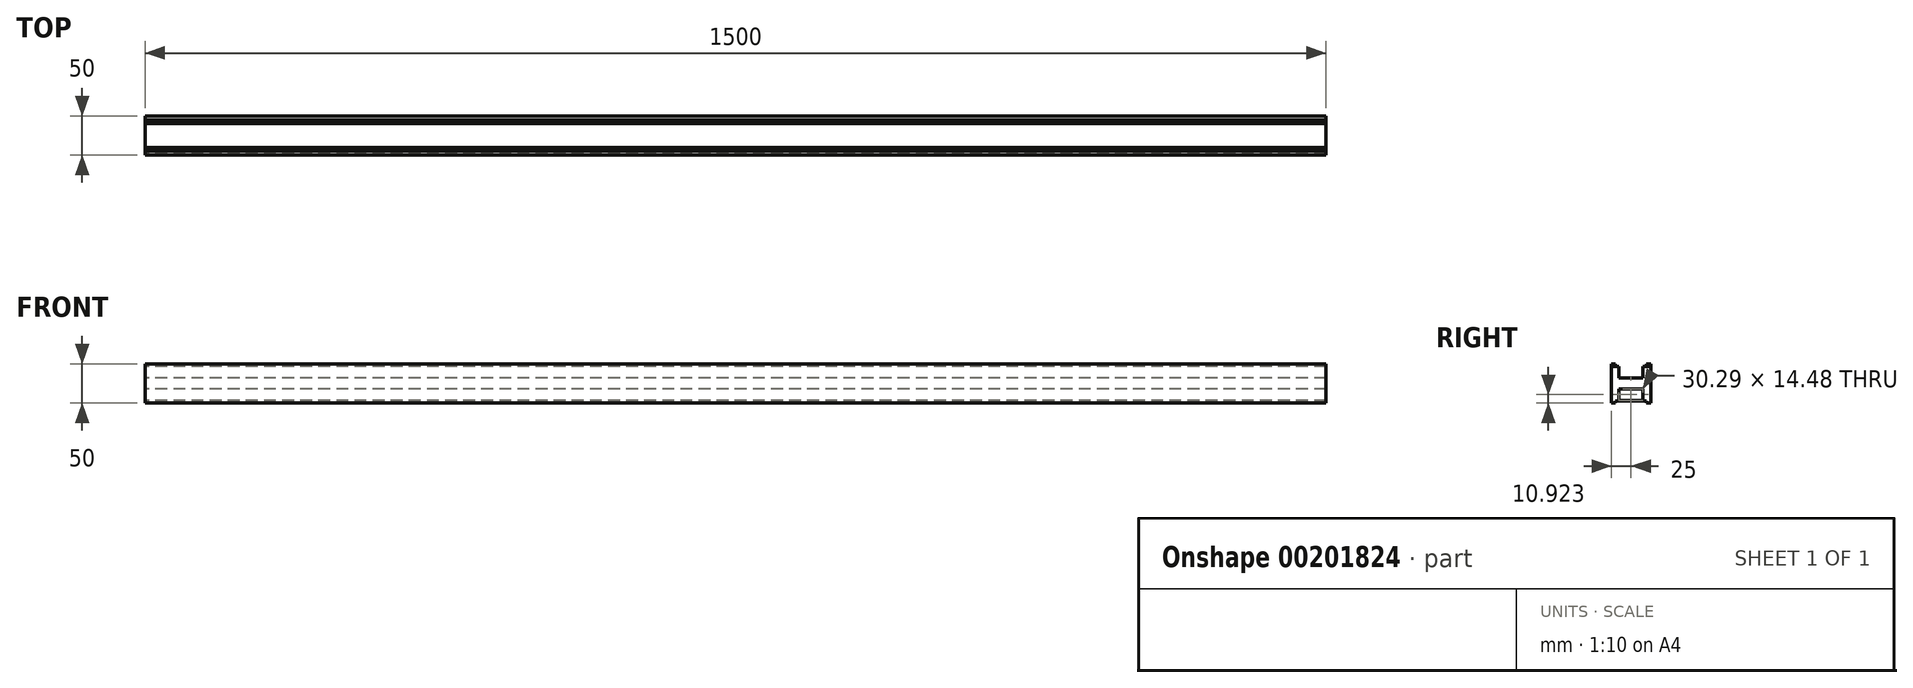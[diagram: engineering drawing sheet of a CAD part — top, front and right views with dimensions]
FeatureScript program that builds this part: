
annotation { "Feature Type Name" : "Feature", "Feature Type Description" : "" }
export const myFeature = defineFeature(function(context is Context, id is Id, definition is map)
    precondition{}
    {
        {
            var Q0;
            Q0=qCreatedBy(makeId("Right.planeOp"),FACE);
            var sketch = newSketch(context, id + "F0", { "sketchPlane" : qUnion([Q0])});
            skLineSegment(sketch, "E0.bottom", {"start": v(25, -25) * mm, "end": v(-25, -25) * mm});
            skLineSegment(sketch, "E0.top", {"start": v(25, 25) * mm, "end": v(-25, 25) * mm});
            skLineSegment(sketch, "E0.left", {"start": v(25, -25) * mm, "end": v(25, 25) * mm});
            skLineSegment(sketch, "E0.right", {"start": v(-25, -25) * mm, "end": v(-25, 25) * mm});
            skPoint(sketch, "E0.middle", {"position": v(0, 0) * mm});
            skSolve(sketch);
        }
        {
            var Q0;
            Q0 = qSketchRegion(id + "F0", true);
            var Q1;
            Q1=makeQuery(id+"F0.imprint","IMPRINT",FACE,{"disambiguationData":[TD([[makeQuery(id+"F0.imprint","IMPRINT",EDGE,{"derivedFrom":sQuery(id+"F0.wireOp",EDGE,"E0.bottom")}),-1.0]])]});
            extrude(context, id + "F1", {"entities" : qUnion([Q0, Q1]), "depth" : 1500 * mm, "offsetDistance" : 25 * mm});
        }
        {
            var Q0;
            Q0=makeQuery(id+"F1.opExtrude","CAP_FACE",FACE,{"disambiguationData":[OSD([sQuery(id+"F0.wireOp",EDGE,"E0.bottom"),sQuery(id+"F0.wireOp",EDGE,"E0.top"),sQuery(id+"F0.wireOp",EDGE,"E0.left"),sQuery(id+"F0.wireOp",EDGE,"E0.right")])],"isStart":true});
            var sketch = newSketch(context, id + "F2", { "sketchPlane" : qUnion([Q0])});
            skLineSegment(sketch, "E1.bottom", {"start": v(19.61, 22.47) * mm, "end": v(-19.61, 22.47) * mm});
            skLineSegment(sketch, "E1.top", {"start": v(19.61, 27.53) * mm, "end": v(-19.61, 27.53) * mm});
            skLineSegment(sketch, "E1.left", {"start": v(19.61, 22.47) * mm, "end": v(19.61, 27.53) * mm});
            skLineSegment(sketch, "E1.right", {"start": v(-19.61, 22.47) * mm, "end": v(-19.61, 27.53) * mm});
            skPoint(sketch, "E1.middle", {"position": v(0, 25) * mm});
            skLineSegment(sketch, "E2.bottom", {"start": v(23.38, 21.32) * mm, "end": v(-23.38, 21.32) * mm});
            skLineSegment(sketch, "E2.top", {"start": v(23.38, 23.62) * mm, "end": v(-23.38, 23.62) * mm});
            skLineSegment(sketch, "E2.left", {"start": v(23.38, 21.32) * mm, "end": v(23.38, 23.62) * mm});
            skLineSegment(sketch, "E2.right", {"start": v(-23.38, 21.32) * mm, "end": v(-23.38, 23.62) * mm});
            skPoint(sketch, "E2.middle", {"position": v(0, 22.47) * mm});
            skLineSegment(sketch, "E3.bottom", {"start": v(15.14, 6.84) * mm, "end": v(-15.14, 6.84) * mm});
            skLineSegment(sketch, "E3.top", {"start": v(15.14, 21.32) * mm, "end": v(-15.14, 21.32) * mm});
            skLineSegment(sketch, "E3.left", {"start": v(15.14, 6.84) * mm, "end": v(15.14, 21.32) * mm});
            skLineSegment(sketch, "E3.right", {"start": v(-15.14, 6.84) * mm, "end": v(-15.14, 21.32) * mm});
            skPoint(sketch, "E3.middle", {"position": v(0, 14.08) * mm});
            skPoint(sketch, "E3.middle.positionSnap0", {"position": v(0, 21.32) * mm});
            skPoint(sketch, "E3.centerSnap0", {"position": v(0, 21.32) * mm});
            skLineSegment(sketch, "E4", {"start": v(-25, 0) * mm, "end": v(25, 0) * mm, "construction": true});
            skLineSegment(sketch, "E5.MirrorCS", {"start": v(15.14, -6.84) * mm, "end": v(-15.14, -6.84) * mm});
            skLineSegment(sketch, "E6.MirrorCS", {"start": v(-15.14, -6.84) * mm, "end": v(-15.14, -21.32) * mm});
            skLineSegment(sketch, "E7.MirrorCS", {"start": v(15.14, -6.84) * mm, "end": v(15.14, -21.32) * mm});
            skLineSegment(sketch, "E8.MirrorCS", {"start": v(23.38, -21.32) * mm, "end": v(-23.38, -21.32) * mm});
            skLineSegment(sketch, "E9.MirrorCS", {"start": v(23.38, -21.32) * mm, "end": v(23.38, -23.62) * mm});
            skLineSegment(sketch, "E10.MirrorCS", {"start": v(23.38, -23.62) * mm, "end": v(-23.38, -23.62) * mm});
            skLineSegment(sketch, "E11.MirrorCS", {"start": v(19.61, -22.47) * mm, "end": v(19.61, -27.53) * mm});
            skLineSegment(sketch, "E12.MirrorCS", {"start": v(19.61, -27.53) * mm, "end": v(-19.61, -27.53) * mm});
            skLineSegment(sketch, "E13.MirrorCS", {"start": v(-19.61, -22.47) * mm, "end": v(-19.61, -27.53) * mm});
            skLineSegment(sketch, "E14.MirrorCS", {"start": v(-23.38, -21.32) * mm, "end": v(-23.38, -23.62) * mm});
            skLineSegment(sketch, "E15.MirrorCS", {"start": v(19.61, -22.47) * mm, "end": v(-19.61, -22.47) * mm});
            skSolve(sketch);
        }
        {
            var Q0;
            Q0=makeQuery(id+"F2.imprint","IMPRINT",FACE,{"disambiguationData":[TD([[makeQuery(id+"F2.imprint","IMPRINT",EDGE,{"derivedFrom":sQuery(id+"F2.wireOp",EDGE,"E3.bottom")}),-1.0]])]});
            var Q1;
            {var subQ4=sQuery(id+"F2.wireOp",EDGE,"E1.bottom");Q1=makeQuery(id+"F2.imprint","IMPRINT",FACE,{"disambiguationData":[TD([[makeQuery(id+"F2.imprint","IMPRINT",EDGE,{"derivedFrom":subQ4}),1.0]])]});}
            var Q2;
            {var subQ0=sQuery(id+"F2.wireOp",EDGE,"E1.bottom");Q2=makeQuery(id+"F2.imprint","IMPRINT",FACE,{"disambiguationData":[TD([[makeQuery(id+"F2.imprint","IMPRINT",EDGE,{"derivedFrom":subQ0}),-1.0]])]});}
            var Q3;
            {var subQ0=sQuery(id+"F2.wireOp",EDGE,"E2.top");var subQ1=sQuery(id+"F2.wireOp",EDGE,"E1.left");var subQ2=makeQuery(id+"F2.imprint","INTERSECT",VERTEX,{"derivedFrom":[subQ1,subQ0]});Q3=makeQuery(id+"F2.imprint","IMPRINT",FACE,{"disambiguationData":[TD([[makeQuery(id+"F2.imprint","IMPRINT",EDGE,{"disambiguationData":[TD([[subQ2,-1.0]])],"derivedFrom":subQ1}),1.0]])]});}
            var Q4;
            {var subQ0=sQuery(id+"F2.wireOp",EDGE,"E11.MirrorCS");var subQ1=sQuery(id+"F2.wireOp",EDGE,"E10.MirrorCS");var subQ2=makeQuery(id+"F2.imprint","INTERSECT",VERTEX,{"derivedFrom":[subQ1,subQ0]});Q4=makeQuery(id+"F2.imprint","IMPRINT",FACE,{"disambiguationData":[TD([[makeQuery(id+"F2.imprint","IMPRINT",EDGE,{"disambiguationData":[TD([[subQ2,-1.0]])],"derivedFrom":subQ1}),1.0]])]});}
            var Q5;
            {var subQ5=sQuery(id+"F2.wireOp",EDGE,"E15.MirrorCS");Q5=makeQuery(id+"F2.imprint","IMPRINT",FACE,{"disambiguationData":[TD([[makeQuery(id+"F2.imprint","IMPRINT",EDGE,{"derivedFrom":subQ5}),1.0]])]});}
            var Q6;
            {var subQ0=sQuery(id+"F2.wireOp",EDGE,"E9.MirrorCS");Q6=makeQuery(id+"F2.imprint","IMPRINT",FACE,{"disambiguationData":[TD([[makeQuery(id+"F2.imprint","IMPRINT",EDGE,{"derivedFrom":subQ0}),-1.0]])]});}
            var Q7;
            Q7=makeQuery(id+"F2.imprint","IMPRINT",FACE,{"disambiguationData":[TD([[makeQuery(id+"F2.imprint","IMPRINT",EDGE,{"derivedFrom":sQuery(id+"F2.wireOp",EDGE,"E5.MirrorCS")}),1.0]])]});
            extrude(context, id + "F3", {"entities" : qUnion([Q0, Q1, Q2, Q3, Q4, Q5, Q6, Q7]), "operationType" : NewBodyOperationType.REMOVE, "endBound" : BoundingType.THROUGH_ALL, "oppositeDirection" : true, "depth" : 25 * mm, "offsetDistance" : 25 * mm});
        }
    });
